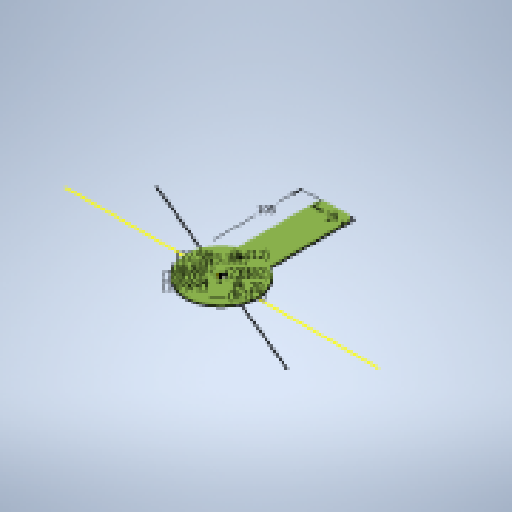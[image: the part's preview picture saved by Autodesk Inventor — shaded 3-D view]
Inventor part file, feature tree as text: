
AUTODESK INVENTOR PART (.ipt)
format: ipt  version: 2023 (Build 270158000, 158)  size: 172,544 bytes
history: native  units: mm
features: sketch x1, extrude x1, fillet x1
ambient origin geometry x8: Origin, YZ Plane, XZ Plane, XY Plane, X Axis, Y Axis, Z Axis, Center Point
bodies: Solid1 (feature_tree)
feature tree (3):
  sketch  "Sketch1"  dims[d0=65.0mm d1=8.0mm d2=1.6mm d3=0.0mm d4=29.0mm d6=24.0mm d8=3.2mm d9=30.0mm d11=360.0deg d13=5.0mm d14=135.0deg d15=20.0mm d16=14.0mm d17=22.5deg d18=6.211657mm d19=23.18222mm d20=16.970563mm d21=16.970563mm d22=23.18222mm d23=6.211657mm d24=105.0mm]
  extrude  "Extrusion1"  Depth=5.0mm
  fillet  "Fillet1"  Radius=1.6mm
